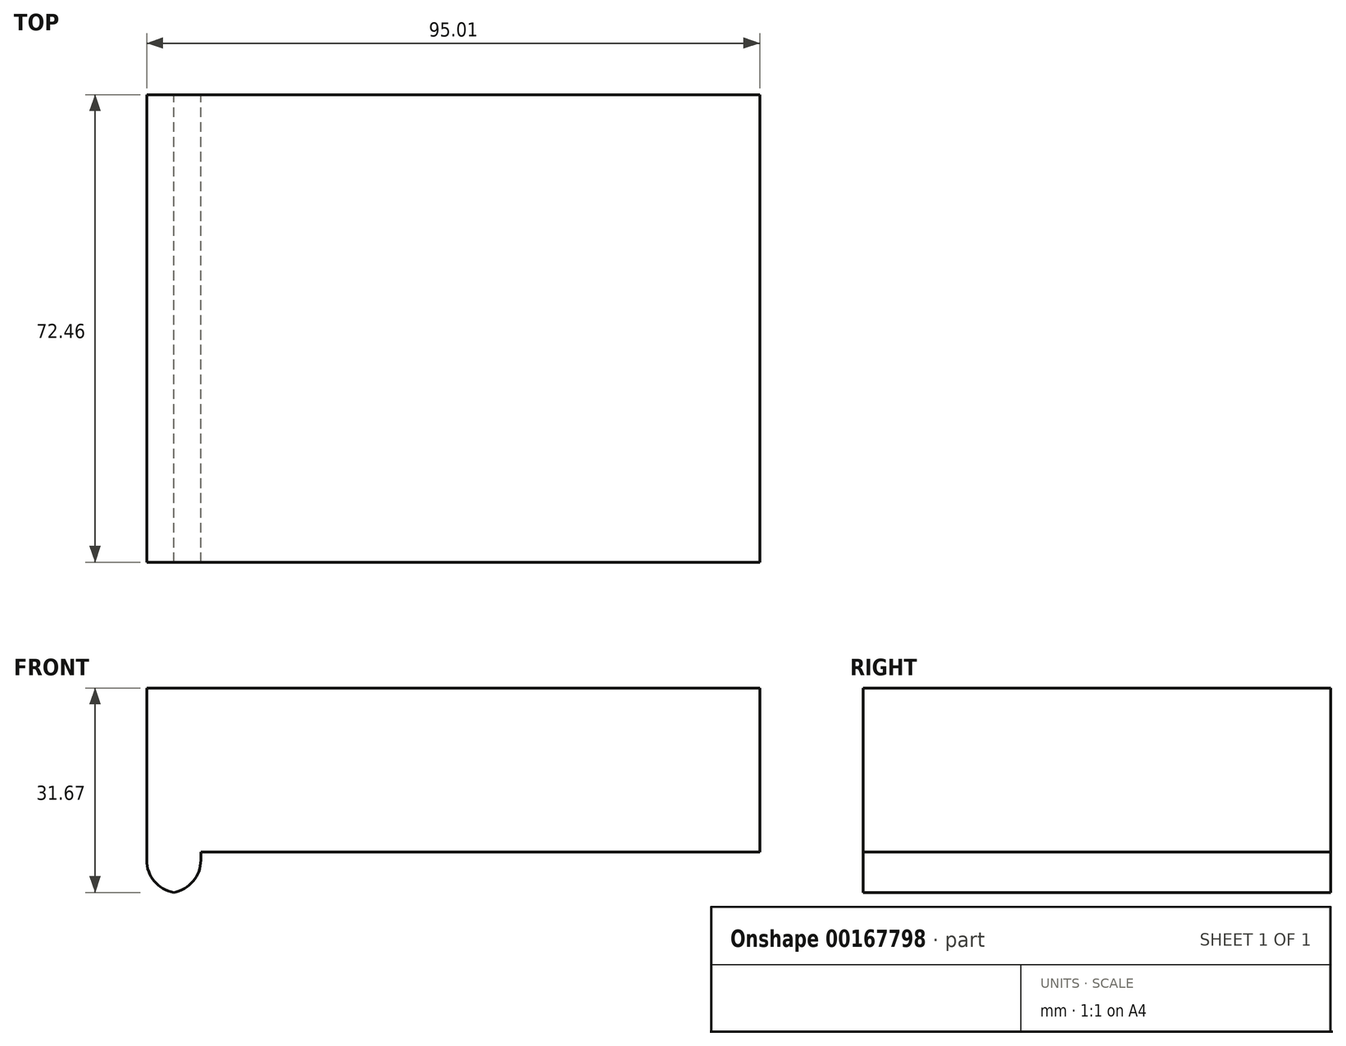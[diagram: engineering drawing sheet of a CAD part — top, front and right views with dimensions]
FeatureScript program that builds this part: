
annotation { "Feature Type Name" : "Feature", "Feature Type Description" : "" }
export const myFeature = defineFeature(function(context is Context, id is Id, definition is map)
    precondition{}
    {
        {
            var Q0;
            Q0=qCreatedBy(makeId("Top.planeOp"),FACE);
            var sketch = newSketch(context, id + "F0", { "sketchPlane" : qUnion([Q0])});
            skLineSegment(sketch, "E0.bottom", {"start": v(-71.4, -30.04) * mm, "end": v(23.6, -30.04) * mm});
            skLineSegment(sketch, "E0.top", {"start": v(-71.4, 42.42) * mm, "end": v(23.6, 42.42) * mm});
            skLineSegment(sketch, "E0.left", {"start": v(-71.4, -30.04) * mm, "end": v(-71.4, 42.42) * mm});
            skLineSegment(sketch, "E0.right", {"start": v(23.6, -30.04) * mm, "end": v(23.6, 42.42) * mm});
            skSolve(sketch);
        }
        {
            var Q0;
            Q0 = qSketchRegion(id + "F0", true);
            extrude(context, id + "F1", {"entities" : qUnion([Q0]), "depth" : 25.4 * mm});
        }
        {
            var Q0;
            Q0=makeQuery(id+"F1.opExtrude","CAP_FACE",FACE,{"disambiguationData":[OSD([sQuery(id+"F0.wireOp",EDGE,"E0.bottom"),sQuery(id+"F0.wireOp",EDGE,"E0.top"),sQuery(id+"F0.wireOp",EDGE,"E0.left"),sQuery(id+"F0.wireOp",EDGE,"E0.right")])],"isStart":true});
            var sketch = newSketch(context, id + "F2", { "sketchPlane" : qUnion([Q0])});
            skLineSegment(sketch, "E1.bottom", {"start": v(-71.4, 30.04) * mm, "end": v(-63.01, 30.04) * mm});
            skLineSegment(sketch, "E1.top", {"start": v(-71.4, -42.42) * mm, "end": v(-63.01, -42.42) * mm});
            skLineSegment(sketch, "E1.left", {"start": v(-71.4, 30.04) * mm, "end": v(-71.4, -42.42) * mm});
            skLineSegment(sketch, "E1.right", {"start": v(-63.01, 30.04) * mm, "end": v(-63.01, -42.42) * mm});
            skSolve(sketch);
        }
        {
            var Q0;
            Q0 = qSketchRegion(id + "F2", true);
            extrude(context, id + "F3", {"entities" : qUnion([Q0]), "operationType" : NewBodyOperationType.ADD, "depth" : 6.35 * mm});
        }
        {
            var Q0;
            Q0=makeQuery(id+"F3.opExtrude","CAP_EDGE",EDGE,{"disambiguationData":[OSD([sQuery(id+"F2.wireOp",EDGE,"E1.right")])],"isStart":false});
            var Q1;
            Q1=makeQuery(id+"F3.opExtrude","CAP_EDGE",EDGE,{"disambiguationData":[OSD([sQuery(id+"F2.wireOp",EDGE,"E1.left")])],"isStart":false});
            fillet(context, id + "F4", {"entities" : qUnion([Q0, Q1]), "radius" : 5.08 * mm, "tangentPropagation" : true, "allowEdgeOverflow" : false});
        }
    });
